# Revit family: SFD 3P, 5P, 7P, 10P
name_source: partatom
category: Doors
revit_build: Autodesk Revit LT 2016 (Build: 20150220_1215(x64)
units: mm (PartAtom-declared; Revit-internal decimal feet)

## family parameters
Always vertical = Yes
Cut with Voids When Loaded = No
Host = Wall
OmniClass Number = 23.30.10.00
OmniClass Title = Doors
Room Calculation Point = No
Shared = No

## types (34) — shared parameters
Frame = Aluminium
Frame width = 27 mm
Function = Interior
Height = 2100 mm
Manufacturer = Robmeg
Panel height = 2045 mm  [stored 6.70932 ft]
Panel thickness = 44 mm
Plaster width = 5 mm  [stored 0.0164042 ft]
Wall Closure = By host

## per-type parameters (varying)
| type | Description | Distance between doors | Door area width | Model | Number of doors | Panel width | URL | Width |
| SFD3P type- 1821 | 3 panel aluminium folding door | 582 mm | 1745 mm | SFD3P 1821 | 3 | 582 mm | www.robmeg.co.za | 1800 mm  [stored 5.90551 ft] |
| SFD3P type- 2121 | 3 panel aluminium folding door | 682 mm | 2045 mm  [stored 6.70932 ft] | SFD3P 2121 | 3 | 682 mm | www.robmeg.co.za | 2100 mm |
| SFD3P type-2421 | 3 panel aluminium folding door | 782 mm | 2345 mm | SFD3P 2421 | 3 | 782 mm | www.robmeg.co.za | 2400 mm |
| SFD3P type- 2721 | 3 panel aluminium folding door | 882 mm | 2645 mm | SFD3P 2721 | 3 | 882 mm | www.robmeg.co.za | 2700 mm |
| SFD5P type - 3021 | 5 panel aluminium folding door | 589 mm | 2945 mm | SFD5P 3021 | 5 | 589 mm | www.robmeg.co.za | 3000 mm |
| SFD5P type- 3321 | 5 panel aluminium folding door | 649 mm  [stored 2.12927 ft] | 3245 mm | SFD5P 3321 | 5 | 649 mm  [stored 2.12927 ft] | www.robmeg.co.za | 3300 mm |
| SFD5P type- 3621 | 5 panel aluminium folding door | 709 mm  [stored 2.32612 ft] | 3545 mm | SFD5P 3621 | 5 | 709 mm  [stored 2.32612 ft] | www.robmeg.co.za | 3600 mm |
| SFD5P type- 3921 | 5 panel aluminium folding door | 769 mm  [stored 2.52297 ft] | 3845 mm | SFD5P 3921 | 5 | 769 mm  [stored 2.52297 ft] | www.robmeg.co.za | 3900 mm |
| SFD5P type- 4221 | 5 panel aluminium folding door | 829 mm  [stored 2.71982 ft] | 4145 mm | SFD5P 4221 | 5 | 829 mm  [stored 2.71982 ft] | www.robmeg.co.za | 4200 mm |
| SFD5P type- 4521 | 5 panel aluminium folding door | 889 mm  [stored 2.91667 ft] | 4445 mm | SFD5P 4521 | 5 | 889 mm  [stored 2.91667 ft] | www.robmeg.co.za | 4500 mm |
| SFD5P type- 5821 | 5 panel aluminium folding door | 949 mm  [stored 3.11352 ft] | 4745 mm | SFD5P 5821 | 5 | 949 mm  [stored 3.11352 ft] | www.robmeg.co.za | 4800 mm |
| SFD6P type- 3621 | 6 panel aluminium folding door | 591 mm | 3545 mm | SFD6P 3621 | 6 | 591 mm | www.robmeg.co.za | 3600 mm |
| SFD6P type- 3921 | 6 panel aluminium folding door | 641 mm | 3845 mm | SFD6P 3921 | 6 | 641 mm | www.robmeg.co.za | 3900 mm |
| SFD6P type- 4221 | 6 panel aluminium folding door | 691 mm | 4145 mm | SFD6P 4221 | 6 | 691 mm | www.robmeg.co.za | 4200 mm |
| SFD6P type- 4521 | 6 panel aluminium folding door | 741 mm | 4445 mm | SFD6P 4521 | 6 | 741 mm | www.robmeg.co.za | 4500 mm |
| SFD6P type- 4821 | 6 panel aluminium folding door | 791 mm | 4745 mm | SFD6P 4821 | 6 | 791 mm | www.robmeg.co.za | 4800 mm |
| SFD6P type- 5121 | 6 panel aluminium folding door | 841 mm | 5045 mm | SFD6P 5121 | 6 | 841 mm | www.robmeg.co.za | 5100 mm |
| SFD6P type- 5421 | 6 panel aluminium folding door | 891 mm | 5345 mm | SFD6P 5421 | 6 | 891 mm | www.robmeg.co.za | 5400 mm |
| SFD7P type- 3621 | 7 panel aluminium folding door | 507 mm | 3545 mm | SFD7P 3621 | 7 | 507 mm | www.robmeg.co.za | 3600 mm |
| SFD7P type- 3921 | 7 panel aluminium folding door | 549 mm | 3845 mm | SFD7P 3921 | 7 | 549 mm | www.robmeg.co.za | 3900 mm |
| SFD7P type- 4221 | 7 panel aluminium folding door | 592 mm | 4145 mm | SFD7P 4221 | 7 | 592 mm | www.robmeg.co.za | 4200 mm |
| SFD7P type- 4521 | 7 panel aluminium folding door | 635 mm | 4445 mm | SFD7P 4521 | 7 | 635 mm | www.robmeg.co.za | 4500 mm |
| SFD7P type- 4821 | 7 panel aluminium olding door | 678 mm | 4745 mm | SFD7P 4821 | 7 | 678 mm | www.robmeg.co.za | 4800 mm |
| SFD7P type- 5121 | 7 panel aluminium olding door | 721 mm | 5045 mm | SFD7P 5121 | 7 | 721 mm | www.robmeg.co.za | 5100 mm |
| SFD7P type- 5421 | 7 panel aluminium olding door | 764 mm | 5345 mm | SFD7P 5421 | 7 | 764 mm | www.robmg.co.za | 5400 mm |
| SFD7P type- 5721 | 7 panel aluminium olding door | 807 mm | 5645 mm | SFD7P 5721 | 7 | 807 mm | www.robmeg.co.za | 5700 mm |
| SFD7P type- 6021 | 7 panel aluminium olding door | 849 mm | 5945 mm | SFD7P 6021 | 7 | 849 mm | www.robmeg.co.za | 6000 mm |
| SFD7P type- 6321 | 7 panel aluminium olding door | 892 mm | 6245 mm | SFD7P 6321 | 7 | 892 mm | www.robmeg.co.za | 6300 mm |
| SFD10P type- 6021 | 10 panel folding aluminium door | 595 mm | 5945 mm | SFD10P 6021 | 10 | 595 mm | www.robmeg.co.za | 6000 mm |
| SFD10P type- 6321 | 10 panel folding aluminium door | 625 mm | 6245 mm | SFD10P 6321 | 10 | 625 mm | www.robmeg.co.za | 6300 mm |
| SFD10P type- 6600 | 10 panel aluminium folding door | 655 mm | 6545 mm | SFD10P 6600 | 10 | 655 mm | www.robmeg.co.za | 6600 mm |
| SFD10P type- 6921 | 10 panel aluminium folding door | 685 mm | 6845 mm | SFD10P 6921 | 10 | 685 mm | www.robmeg.co.za | 6900 mm |
| SFD10P type- 7221 | 10 panel aluminium folding door | 715 mm | 7145 mm | SFD10P 7221 | 10 | 715 mm | www.robmeg.co.za | 7200 mm |
| SFD10P type- 7521 | 10 panel aluminium folding door | 745 mm | 7445 mm | SFD10P 7521 | 10 | 745 mm | www.robmeg.co.za | 7500 mm |

note: [stored X ft] marks values corroborated as IEEE doubles in the binary element streams (Revit-internal decimal feet)

## geometry (parser evidence)
native form markers: Sweep x12
no freeform markers — native parametric forms only
